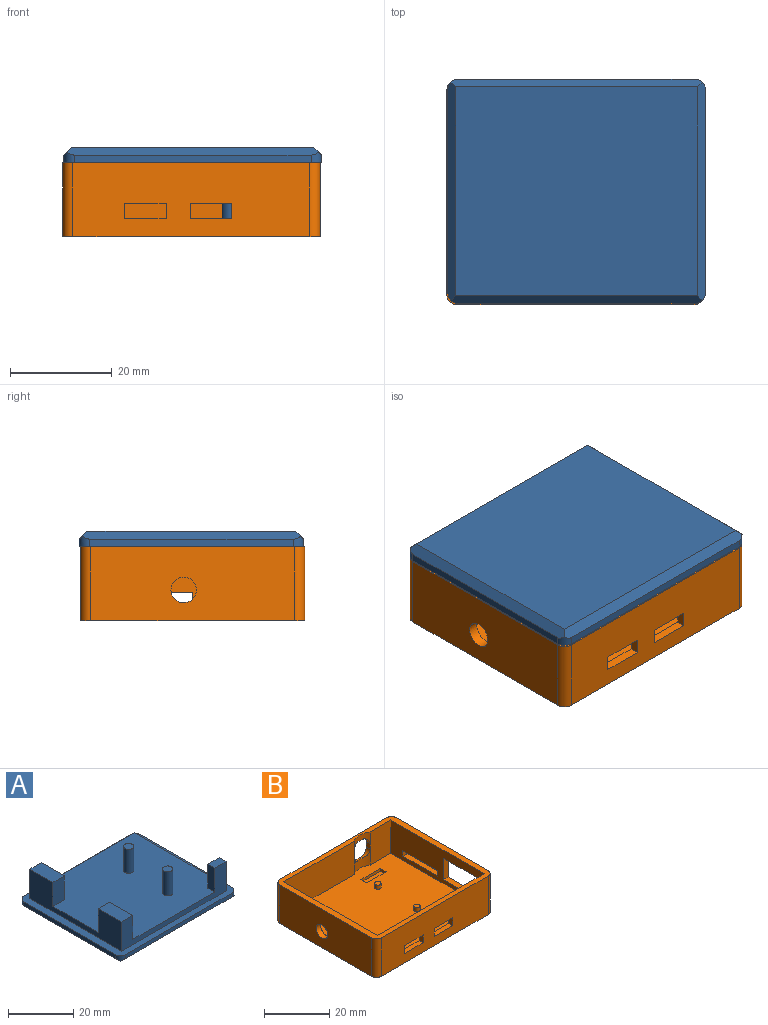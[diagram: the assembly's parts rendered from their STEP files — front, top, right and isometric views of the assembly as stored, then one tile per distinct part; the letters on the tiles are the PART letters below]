
ASSEMBLY  parts=2 mates=1
PART A: 32 faces, bbox 50.5x44x14 mm
  f0: plane 45.5x39.8mm, normal (0,0,1), area 1679.8mm2, adj f7,f8,f9,f10,f15,f16,f18,f19
  f1: plane 50.5x44mm, normal (0,0,1), area 407.7mm2, adj f2,f3,f4,f5,f7,f8,f9,f10
  f2: plane 46.5x1.5mm, normal (0,1,0), area 69.8mm2, adj f1,f11,f28,f31
  f3: plane 40x1.5mm, normal (-1,0,0), area 60mm2, adj f1,f12,f28,f29
  f4: plane 46.5x1.5mm, normal (0,-1,0), area 69.8mm2, adj f1,f14,f29,f30
  f5: plane 40x1.5mm, normal (1,0,0), area 60mm2, adj f1,f13,f30,f31
  f6: plane 47.5x41mm, normal (0,0,-1), area 1947.5mm2, adj f11,f12,f13,f14
  f7: plane 45.5x11mm, normal (0,1,0), area 136mm2, adj f0,f1,f8,f10,f16,f17
  f8: plane 39.8x11mm, normal (-1,0,0), area 259.6mm2, adj f0,f1,f7,f9,f15,f17,f18,f20
  f9: plane 45.5x11mm, normal (0,-1,0), area 181mm2, adj f0,f1,f8,f10,f19,f20,f22,f23
  f10: plane 39.8x11mm, normal (1,0,0), area 106.6mm2, adj f0,f1,f7,f9,f21,f23
  f11: plane 49.33x1.5mm, normal (0,0.71,-0.71), area 102.7mm2, adj f2,f6,f12,f13,f28,f31
  f12: plane 42.83x1.5mm, normal (-0.71,0,-0.71), area 88.9mm2, adj f3,f6,f11,f14,f28,f29
  f13: plane 42.83x1.5mm, normal (0.71,0,-0.71), area 88.9mm2, adj f5,f6,f11,f14,f30,f31
  f14: plane 49.33x1.5mm, normal (0,-0.71,-0.71), area 102.7mm2, adj f4,f6,f12,f13,f29,f30
  f15: plane 9x5mm, normal (0,-1,0), area 45mm2, adj f0,f8,f16,f17
  f16: plane 10x9mm, normal (1,0,0), area 90mm2, adj f0,f7,f15,f17
  f17: plane 10x5mm, normal (0,0,1), area 50mm2, adj f7,f8,f15,f16
  f18: plane 9x5mm, normal (0,1,0), area 45mm2, adj f0,f8,f19,f20
  f19: plane 10x9mm, normal (1,0,0), area 90mm2, adj f0,f9,f18,f20
  f20: plane 10x5mm, normal (0,0,1), area 50mm2, adj f8,f9,f18,f19
  f21: plane 9x5mm, normal (0,1,0), area 45mm2, adj f0,f10,f22,f23
  f22: plane 9x3mm, normal (-1,0,0), area 27mm2, adj f0,f9,f21,f23
  f23: plane 5x3mm, normal (0,0,1), area 15mm2, adj f9,f10,f21,f22
  f24: cylinder r=1.6mm len=9mm, axis (0,0,-1), area 90.5mm2, adj f0,f25
  f25: plane 3.2x3.2mm, normal (0,0,1), area 8mm2, adj f24
  f26: cylinder r=1.6mm len=9mm, axis (0,0,-1), area 90.5mm2, adj f0,f27
  f27: plane 3.2x3.2mm, normal (0,0,1), area 8mm2, adj f26
  f28: cylinder r=2mm len=2.09mm, axis (0,0,1), area 5.3mm2, adj f1,f2,f3,f11,f12
  f29: cylinder r=2mm len=2.09mm, axis (0,0,-1), area 5.3mm2, adj f1,f3,f4,f12,f14
  f30: cylinder r=2mm len=2.09mm, axis (0,0,1), area 5.3mm2, adj f1,f4,f5,f13,f14
  f31: cylinder r=2mm len=2.09mm, axis (0,0,-1), area 5.3mm2, adj f1,f2,f5,f11,f13
PART B: 52 faces, bbox 50.5x44x14.5 mm
  f0: plane 12.5x9mm, normal (0,-1,0), area 112.5mm2, adj f13,f21,f33,f35,f41,f42
  f1: plane 3x1.75mm, normal (1,0,0), area 5.2mm2, adj f11,f16,f22,f39
  f2: plane 3x1.75mm, normal (-1,0,0), area 5.2mm2, adj f11,f16,f22,f39
  f3: plane 3x1.75mm, normal (1,0,0), area 5.2mm2, adj f12,f16,f22,f38
  f4: plane 3x1.75mm, normal (-1,0,0), area 5.2mm2, adj f12,f16,f22,f38
  f5: plane 8x2mm, normal (0,1,0), area 16mm2, adj f10,f17,f21,f37
  f6: plane 8x2mm, normal (0,-1,0), area 16mm2, adj f10,f17,f21,f37
  f7: plane 2x2mm, normal (0,-1,0), area 4mm2, adj f9,f17,f21,f36
  f8: plane 2x2mm, normal (0,1,0), area 4mm2, adj f9,f17,f21,f36
  f9: plane 15x2mm, normal (0,0,1), area 30mm2, adj f7,f8,f17,f21
  f10: plane 16x2mm, normal (0,0,1), area 32mm2, adj f5,f6,f17,f21
  f11: plane 8.2x1.75mm, normal (0,0,1), area 14.3mm2, adj f1,f2,f16,f22
  f12: plane 8.2x1.75mm, normal (0,0,1), area 14.3mm2, adj f3,f4,f16,f22
  f13: plane 46.5x41.5mm, normal (0,0,1), area 1860.5mm2, adj f0,f19,f20,f21,f22,f23,f24,f25
  f14: plane 46.5x14.5mm, normal (0,1,0), area 629.9mm2, adj f18,f32,f33,f34,f35,f43,f44,f45
  f15: plane 40x14.5mm, normal (-1,0,0), area 560.4mm2, adj f18,f35,f40,f48,f49
  f16: plane 46.5x14.5mm, normal (0,-1,0), area 625.1mm2, adj f1,f2,f3,f4,f11,f12,f18,f35
  f17: plane 40x14.5mm, normal (1,0,0), area 422mm2, adj f5,f6,f7,f8,f9,f10,f18,f35
  f18: plane 50.5x44mm, normal (0,0,-1), area 2218.6mm2, adj f14,f15,f16,f17,f48,f49,f50,f51
  f19: plane 40.5x12.5mm, normal (1,0,0), area 486.6mm2, adj f13,f20,f22,f35,f40
  f20: plane 30.5x12.5mm, normal (0,-1,0), area 381.3mm2, adj f13,f19,f32,f35,f41,f42
  f21: plane 40.5x12.5mm, normal (-1,0,0), area 348.3mm2, adj f0,f5,f6,f7,f8,f9,f10,f13
  f22: plane 46.5x12.5mm, normal (0,1,0), area 532.1mm2, adj f1,f2,f3,f4,f11,f12,f13,f19
  f23: plane 2.5x1mm, normal (-1,0,0), area 2.5mm2, adj f13,f24,f26,f27
  f24: plane 8.5x1mm, normal (0,-1,0), area 8.5mm2, adj f13,f23,f25,f27
  f25: plane 2.5x1mm, normal (1,0,0), area 2.5mm2, adj f13,f24,f26,f27
  f26: plane 8.5x1mm, normal (0,1,0), area 8.5mm2, adj f13,f23,f25,f27
  f27: plane 8.5x2.5mm, normal (0,0,1), area 21.2mm2, adj f23,f24,f25,f26
  f28: cylinder r=1mm len=2mm, axis (0,0,-1), area 9.4mm2, adj f13,f29
  f29: plane 2x2mm, normal (0,0,1), area 3.1mm2, adj f28
  f30: cylinder r=1mm len=2mm, axis (0,0,-1), area 9.4mm2, adj f13,f31
  f31: plane 2x2mm, normal (0,0,1), area 3.1mm2, adj f30
  f32: plane 2.1x1.75mm, normal (1,0,0), area 3.7mm2, adj f14,f20,f45,f47
  f33: plane 2.1x1.75mm, normal (-1,0,0), area 3.7mm2, adj f0,f14,f44,f46
  f34: plane 2x0.83mm, normal (0,0,-1), area 1.6mm2, adj f14,f41,f46,f47
  f35: plane 50.5x44mm, normal (0,0,1), area 330.6mm2, adj f0,f14,f15,f16,f17,f19,f20,f21
  f36: plane 15x2mm, normal (0,0,-1), area 30mm2, adj f7,f8,f17,f21
  f37: plane 16x2mm, normal (0,0,-1), area 32mm2, adj f5,f6,f17,f21
  f38: plane 8.2x1.75mm, normal (0,0,-1), area 14.3mm2, adj f3,f4,f16,f22
  f39: plane 8.2x1.75mm, normal (0,0,-1), area 14.3mm2, adj f1,f2,f16,f22
  f40: cylinder r=2.5mm len=5mm, axis (-1,0,0), area 31.4mm2, adj f15,f19
  f41: cylinder r=6.62mm len=7mm, axis (0,0,-1), area 17.8mm2, adj f0,f20,f34,f35,f46,f47
  f42: cylinder r=6.62mm len=7mm, axis (0,0,1), area 28.1mm2, adj f0,f13,f20,f43,f44,f45
  f43: plane 2x0.83mm, normal (0,0,1), area 1.6mm2, adj f14,f42,f44,f45
  f44: cylinder r=2.5mm len=2.5mm, axis (0,-1,0), area 5.2mm2, adj f14,f33,f42,f43
  f45: cylinder r=2.5mm len=2.5mm, axis (0,1,0), area 5.2mm2, adj f14,f32,f42,f43
  f46: cylinder r=2.5mm len=2.5mm, axis (0,1,0), area 5.2mm2, adj f14,f33,f34,f41
  f47: cylinder r=2.5mm len=2.5mm, axis (0,-1,0), area 5.2mm2, adj f14,f32,f34,f41
  f48: cylinder r=2mm len=14.5mm, axis (0,0,1), area 45.6mm2, adj f14,f15,f18,f35
  f49: cylinder r=2mm len=14.5mm, axis (0,0,-1), area 45.6mm2, adj f15,f16,f18,f35
  f50: cylinder r=2mm len=14.5mm, axis (0,0,1), area 45.6mm2, adj f16,f17,f18,f35
  f51: cylinder r=2mm len=14.5mm, axis (0,0,-1), area 45.6mm2, adj f14,f17,f18,f35
PLACE A rot(axis=(1,0,0),180deg) t=(-21.99,-5.19,20.73)mm
PLACE B t=(-22.24,-5.44,3.23)mm
MATE fastened A.f24 <-> B.f30  axis (0,0,-1) through (-14.69,-12.19,6.73)mm
